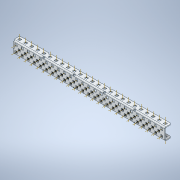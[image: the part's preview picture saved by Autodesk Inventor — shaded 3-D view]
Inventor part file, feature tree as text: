
AUTODESK INVENTOR PART (.ipt)
format: ipt  version: 2020 (Build 240168000, 168)  size: 1,441,792 bytes
history: native  units: in
note: dims shown in document units (in); Inventor stores cm internally (conversion verified against a paired STEP export)
features: other x128, plane x8, pattern_linear x4, split x2, sheet_metal_op x1
ambient origin geometry x8: Origin, YZ Plane, XZ Plane, XY Plane, X Axis, Y Axis, Z Axis, Center Point
bodies: Solid1 (feature_tree)
feature tree (143):
  other  "Work Axis1"
  pattern_linear  "Rectangular Pattern1"  Count1=25 Spacing1=0.5in
  other  "Work Axis72"
  pattern_linear  "Rectangular Pattern2"  Count1=25 Spacing1=0.5in
  pattern_linear  "Rectangular Pattern3"  Count1=25 Spacing1=0.5in
  other  "Work Axis141"
  pattern_linear  "Rectangular Pattern4"  Count1=24 Spacing1=0.5in
  plane  "Work Plane7"
  split  "Split1"
  plane  "Work Plane8"
  split  "Split2"
  plane  "Work Plane1"
  plane  "Work Plane2"
  other  "Work Point1"
  other  "Work Axis2"
  other  "Work Axis3"
  other  "Work Axis4"
  other  "Work Axis5"
  other  "Work Axis6"
  other  "Work Axis7"
  other  "Work Axis8"
  other  "Work Axis9"
  other  "Work Axis10"
  other  "Work Axis11"
  other  "Work Axis12"
  other  "Work Axis13"
  other  "Work Axis14"
  other  "Work Axis15"
  other  "Work Axis16"
  other  "Work Axis17"
  other  "Work Axis18"
  other  "Work Axis19"
  other  "Work Axis20"
  other  "Work Axis21"
  other  "Work Axis22"
  other  "Work Axis23"
  other  "Work Axis24"
  other  "Work Axis25"
  other  "Work Axis36"
  other  "Work Axis37"
  other  "Work Axis38"
  other  "Work Axis39"
  other  "Work Axis40"
  other  "Work Axis41"
  other  "Work Axis42"
  other  "Work Axis43"
  other  "Work Axis44"
  other  "Work Axis45"
  other  "Work Axis46"
  other  "Work Axis47"
  other  "Work Axis48"
  other  "Work Axis49"
  other  "Work Axis50"
  other  "Work Axis51"
  other  "Work Axis52"
  other  "Work Axis53"
  other  "Work Axis54"
  other  "Work Axis55"
  other  "Work Axis56"
  other  "Work Axis57"
  other  "Work Axis58"
  other  "Work Axis59"
  other  "Work Axis60"
  plane  "Work Plane3"
  plane  "Work Plane4"
  other  "Work Point2"
  other  "Work Axis71"
  other  "Work Point3"
  other  "Work Axis73"
  other  "Work Axis74"
  other  "Work Axis75"
  other  "Work Axis76"
  other  "Work Axis77"
  other  "Work Axis78"
  other  "Work Axis79"
  other  "Work Axis80"
  other  "Work Axis81"
  other  "Work Axis82"
  other  "Work Axis83"
  other  "Work Axis84"
  other  "Work Axis85"
  other  "Work Axis86"
  other  "Work Axis87"
  other  "Work Axis88"
  other  "Work Axis89"
  other  "Work Axis90"
  other  "Work Axis91"
  other  "Work Axis92"
  other  "Work Axis93"
  other  "Work Axis94"
  other  "Work Axis95"
  other  "Work Axis96"
  other  "Work Axis107"
  other  "Work Axis108"
  other  "Work Axis109"
  other  "Work Axis110"
  plane  "Work Plane5"
  plane  "Work Plane6"
  other  "Work Point4"
  other  "Work Axis142"
  other  "Work Axis143"
  other  "Work Axis144"
  other  "Work Axis145"
  other  "Work Axis146"
  other  "Work Axis147"
  other  "Work Axis148"
  other  "Work Axis149"
  other  "Work Axis150"
  other  "Work Axis151"
  other  "Work Axis152"
  other  "Work Axis153"
  other  "Work Axis154"
  other  "Work Axis155"
  other  "Work Axis156"
  other  "Work Axis157"
  other  "Work Axis158"
  other  "Work Axis159"
  other  "Work Axis160"
  other  "Work Axis161"
  other  "Work Axis162"
  other  "Work Axis163"
  other  "Work Axis164"
  other  "Work Axis175"
  other  "Work Axis176"
  other  "Work Axis177"
  other  "Work Axis178"
  other  "Work Axis179"
  other  "Work Axis180"
  other  "Work Axis181"
  other  "Work Axis182"
  other  "Work Axis183"
  other  "Work Axis184"
  other  "Work Axis185"
  other  "Work Axis186"
  other  "Work Axis187"
  other  "Work Axis188"
  other  "Work Axis189"
  other  "Work Axis190"
  other  "Work Axis191"
  other  "Work Axis192"
  other  "Work Axis193"
  other  "Work Axis194"
  sheet_metal_op  "Fold1"
